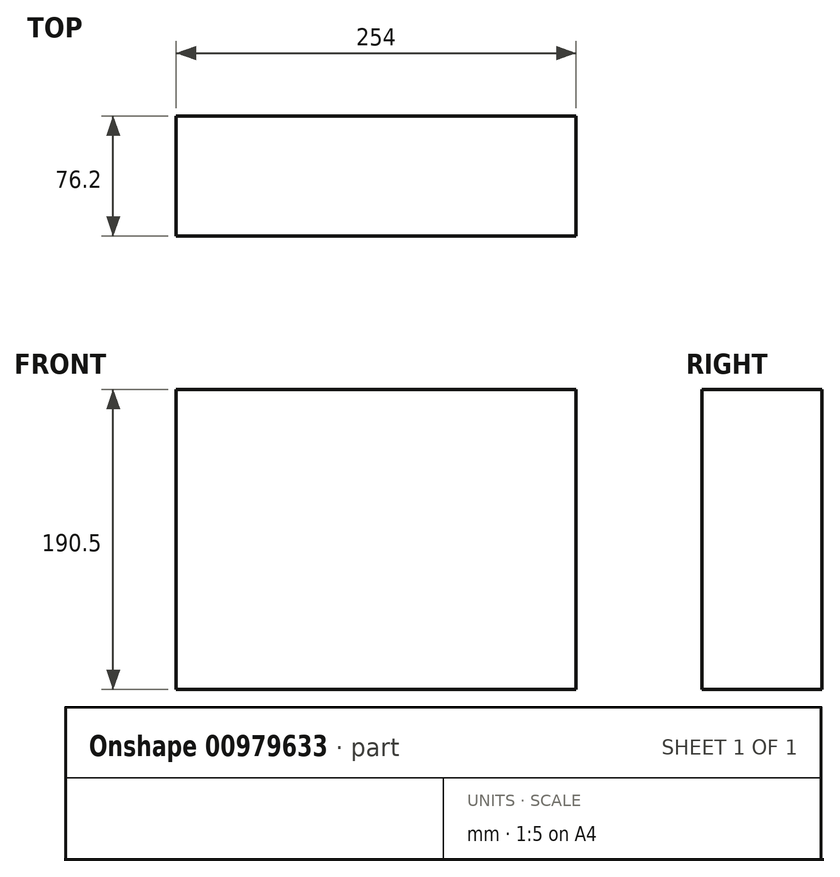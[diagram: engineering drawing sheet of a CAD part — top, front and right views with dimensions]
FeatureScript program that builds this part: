
annotation { "Feature Type Name" : "Feature", "Feature Type Description" : "" }
export const myFeature = defineFeature(function(context is Context, id is Id, definition is map)
    precondition{}
    {
        {
            var Q0;
            Q0=qCreatedBy(makeId("Front.planeOp"),FACE);
            var sketch = newSketch(context, id + "F0", { "sketchPlane" : qUnion([Q0])});
            skLineSegment(sketch, "E0.bottom", {"start": v(127, -95.25) * mm, "end": v(-127, -95.25) * mm});
            skLineSegment(sketch, "E0.top", {"start": v(127, 95.25) * mm, "end": v(-127, 95.25) * mm});
            skLineSegment(sketch, "E0.left", {"start": v(127, -95.25) * mm, "end": v(127, 95.25) * mm});
            skLineSegment(sketch, "E0.right", {"start": v(-127, -95.25) * mm, "end": v(-127, 95.25) * mm});
            skPoint(sketch, "E0.middle", {"position": v(0, 0) * mm});
            skSolve(sketch);
        }
        {
            var Q0;
            Q0 = qSketchRegion(id + "F0", true);
            extrude(context, id + "F1", {"entities" : qUnion([Q0]), "depth" : 76.2 * mm, "offsetDistance" : 25.4 * mm});
        }
    });
